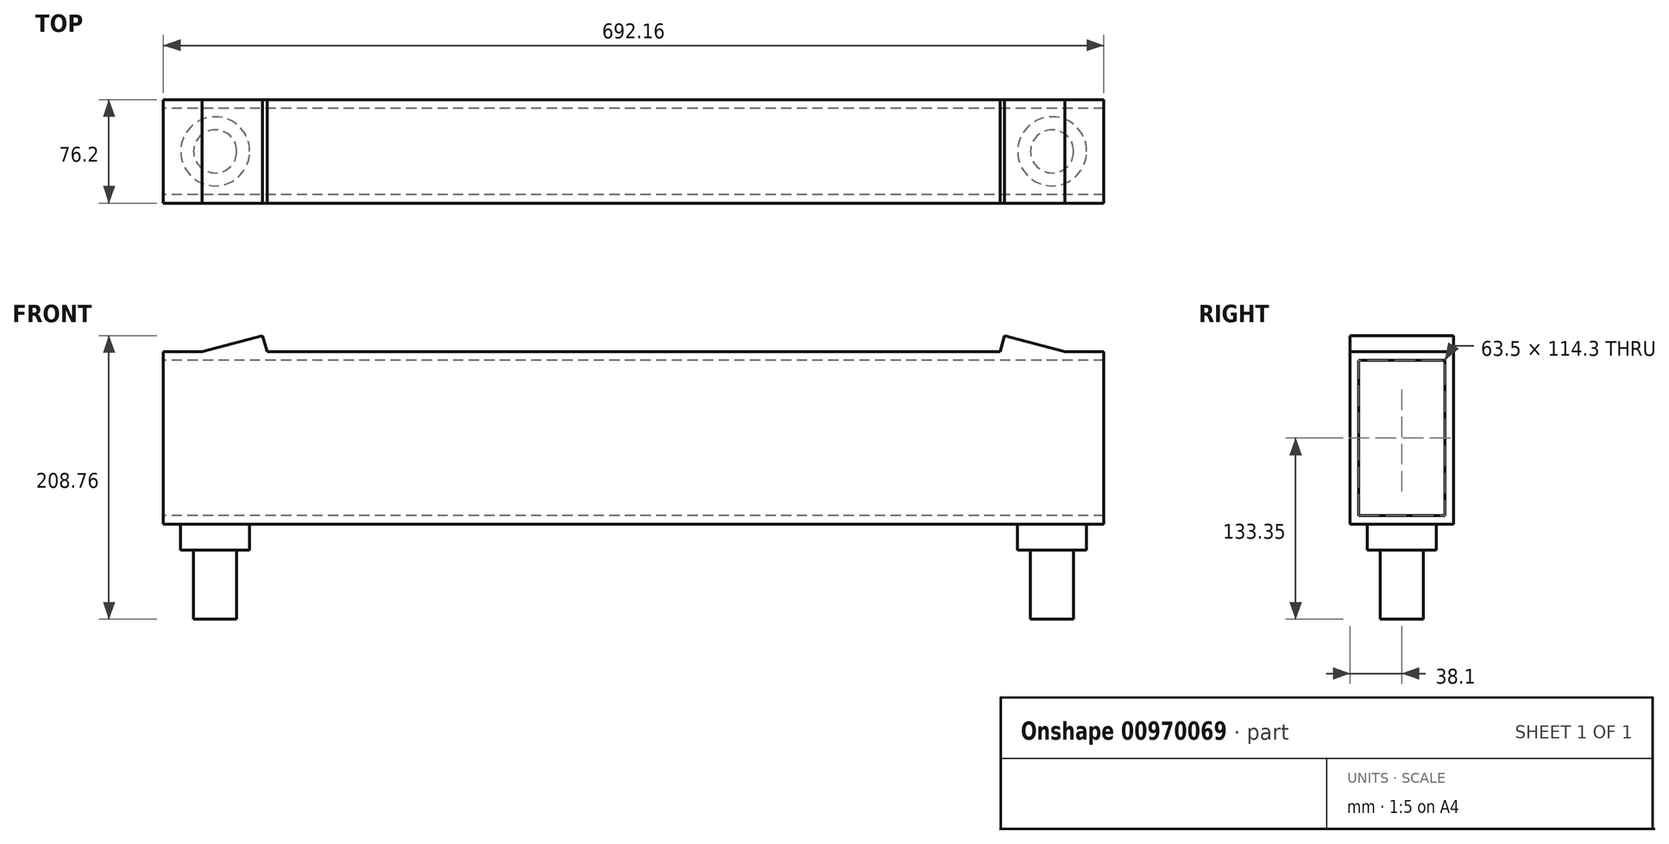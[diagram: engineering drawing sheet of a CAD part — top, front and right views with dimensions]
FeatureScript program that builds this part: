
annotation { "Feature Type Name" : "Feature", "Feature Type Description" : "" }
export const myFeature = defineFeature(function(context is Context, id is Id, definition is map)
    precondition{}
    {
        {
            var Q0;
            Q0=qCreatedBy(makeId("Right.planeOp"),FACE);
            var sketch = newSketch(context, id + "F0", { "sketchPlane" : qUnion([Q0])});
            skLineSegment(sketch, "E0.bottom", {"start": v(38.1, 63.5) * mm, "end": v(-38.1, 63.5) * mm});
            skLineSegment(sketch, "E0.top", {"start": v(38.1, -63.5) * mm, "end": v(-38.1, -63.5) * mm});
            skLineSegment(sketch, "E0.left", {"start": v(38.1, 63.5) * mm, "end": v(38.1, -63.5) * mm});
            skLineSegment(sketch, "E0.right", {"start": v(-38.1, 63.5) * mm, "end": v(-38.1, -63.5) * mm});
            skPoint(sketch, "E0.middle", {"position": v(0, 0) * mm});
            skLineSegment(sketch, "E1.0", {"start": v(-31.75, 57.15) * mm, "end": v(-31.75, -57.15) * mm});
            skLineSegment(sketch, "E1.1", {"start": v(31.75, 57.15) * mm, "end": v(-31.75, 57.15) * mm});
            skLineSegment(sketch, "E1.2", {"start": v(31.75, 57.15) * mm, "end": v(31.75, -57.15) * mm});
            skLineSegment(sketch, "E1.3", {"start": v(31.75, -57.15) * mm, "end": v(-31.75, -57.15) * mm});
            skSolve(sketch);
        }
        {
            var Q0;
            Q0=makeQuery(id+"F0.imprint","IMPRINT",FACE,{"disambiguationData":[TD([[makeQuery(id+"F0.imprint","IMPRINT",EDGE,{"derivedFrom":sQuery(id+"F0.wireOp",EDGE,"E0.bottom")}),1.0]])]});
            extrude(context, id + "F1", {"entities" : qUnion([Q0]), "endBound" : BoundingType.SYMMETRIC, "depth" : 692.15 * mm, "offsetDistance" : 25.4 * mm});
        }
        {
            var Q0;
            Q0=makeQuery(id+"F1.opExtrude","SWEPT_FACE",FACE,{"disambiguationData":[OSD([sQuery(id+"F0.wireOp",EDGE,"E0.top")])]});
            var sketch = newSketch(context, id + "F2", { "sketchPlane" : qUnion([Q0])});
            skCircle(sketch, "E2", {"center": v(-307.98, 0) * mm, "radius": 25.4 * mm});
            skPoint(sketch, "E2.centerSnap0", {"position": v(-346.08, 0) * mm});
            skCircle(sketch, "E3", {"center": v(307.98, 0) * mm, "radius": 25.4 * mm});
            skPoint(sketch, "E3.centerSnap0", {"position": v(346.08, 0) * mm});
            skLineSegment(sketch, "E4", {"start": v(-307.98, 0) * mm, "end": v(307.98, 0) * mm, "construction": true});
            skSolve(sketch);
        }
        {
            var Q0;
            Q0 = qSketchRegion(id + "F2", true);
            extrude(context, id + "F3", {"entities" : qUnion([Q0]), "operationType" : NewBodyOperationType.ADD, "depth" : 19.05 * mm, "offsetDistance" : 25.4 * mm});
        }
        {
            var Q0;
            Q0=qCreatedBy(makeId("Front.planeOp"),FACE);
            var sketch = newSketch(context, id + "F4", { "sketchPlane" : qUnion([Q0])});
            skLineSegment(sketch, "E5", {"start": v(-317.5, 63.5) * mm, "end": v(-273.05, 63.5) * mm});
            skLineSegment(sketch, "E6", {"start": v(-317.5, 63.5) * mm, "end": v(-273.05, 75.41) * mm});
            skLineSegment(sketch, "E7", {"start": v(273.05, 63.5) * mm, "end": v(317.5, 63.5) * mm});
            skLineSegment(sketch, "E8", {"start": v(317.5, 63.5) * mm, "end": v(273.05, 75.41) * mm});
            skLineSegment(sketch, "E9", {"start": v(-273.05, 75.41) * mm, "end": v(273.05, 75.41) * mm, "construction": true});
            skLineSegment(sketch, "E10", {"start": v(0, 0) * mm, "end": v(0, 75.41) * mm, "construction": true});
            skLineSegment(sketch, "E11", {"start": v(-273.05, 75.41) * mm, "end": v(-269.86, 63.5) * mm});
            skLineSegment(sketch, "E12", {"start": v(-269.86, 63.5) * mm, "end": v(-273.05, 63.5) * mm});
            skLineSegment(sketch, "E13", {"start": v(273.05, 63.5) * mm, "end": v(269.86, 63.5) * mm});
            skLineSegment(sketch, "E14", {"start": v(269.86, 63.5) * mm, "end": v(273.05, 75.41) * mm});
            skSolve(sketch);
        }
        {
            var Q0;
            Q0=makeQuery(id+"F4.imprint","IMPRINT",FACE,{"disambiguationData":[TD([[makeQuery(id+"F4.imprint","IMPRINT",EDGE,{"derivedFrom":sQuery(id+"F4.wireOp",EDGE,"E5")}),1.0]])]});
            var Q1;
            Q1=makeQuery(id+"F4.imprint","IMPRINT",FACE,{"disambiguationData":[TD([[makeQuery(id+"F4.imprint","IMPRINT",EDGE,{"derivedFrom":sQuery(id+"F4.wireOp",EDGE,"E7")}),1.0]])]});
            var Q2;
            Q2=makeQuery(id+"F1.opExtrude","SWEPT_FACE",FACE,{"disambiguationData":[OSD([sQuery(id+"F0.wireOp",EDGE,"E0.left")])]});
            var Q3;
            Q3=makeQuery(id+"F1.opExtrude","SWEPT_FACE",FACE,{"disambiguationData":[OSD([sQuery(id+"F0.wireOp",EDGE,"E0.right")])]});
            extrude(context, id + "F5", {"entities" : qUnion([Q0, Q1]), "operationType" : NewBodyOperationType.ADD, "endBound" : BoundingType.UP_TO_SURFACE, "oppositeDirection" : true, "depth" : 25.4 * mm, "endBoundEntityFace" : qUnion([Q2]), "offsetDistance" : 25.4 * mm, "hasSecondDirection" : true, "secondDirectionBound" : SecondDirectionBoundingType.UP_TO_SURFACE, "secondDirectionOppositeDirection" : false, "secondDirectionDepth" : 25.4 * mm, "secondDirectionBoundEntityFace" : qUnion([Q3])});
        }
        {
            var Q0;
            Q0=makeQuery(id+"F3.opExtrude","CAP_FACE",FACE,{"disambiguationData":[OSD([sQuery(id+"F2.wireOp",EDGE,"E2")])],"isStart":false});
            var sketch = newSketch(context, id + "F6", { "sketchPlane" : qUnion([Q0])});
            skCircle(sketch, "E15", {"center": v(-307.98, 0) * mm, "radius": 15.88 * mm});
            skSolve(sketch);
        }
        {
            var Q0;
            Q0=makeQuery(id+"F6.imprint","IMPRINT",FACE,{"disambiguationData":[TD([[makeQuery(id+"F6.imprint","IMPRINT",EDGE,{"derivedFrom":sQuery(id+"F6.wireOp",EDGE,"E15")}),1.0]])]});
            extrude(context, id + "F7", {"entities" : qUnion([Q0]), "depth" : 50.8 * mm, "offsetDistance" : 25.4 * mm});
        }
        {
            var Q0;
            Q0=makeQuery(id+"F7.opExtrude","SWEPT_BODY",BODY,{"disambiguationData":[OSD([sQuery(id+"F6.wireOp",EDGE,"E15")])]});
            var Q1;
            Q1=qCreatedBy(makeId("Right.planeOp"),FACE);
            mirror(context, id + "F8", {"operationType" : NewBodyOperationType.ADD, "entities" : qUnion([Q0]), "mirrorPlane" : qUnion([Q1])});
        }
    });
